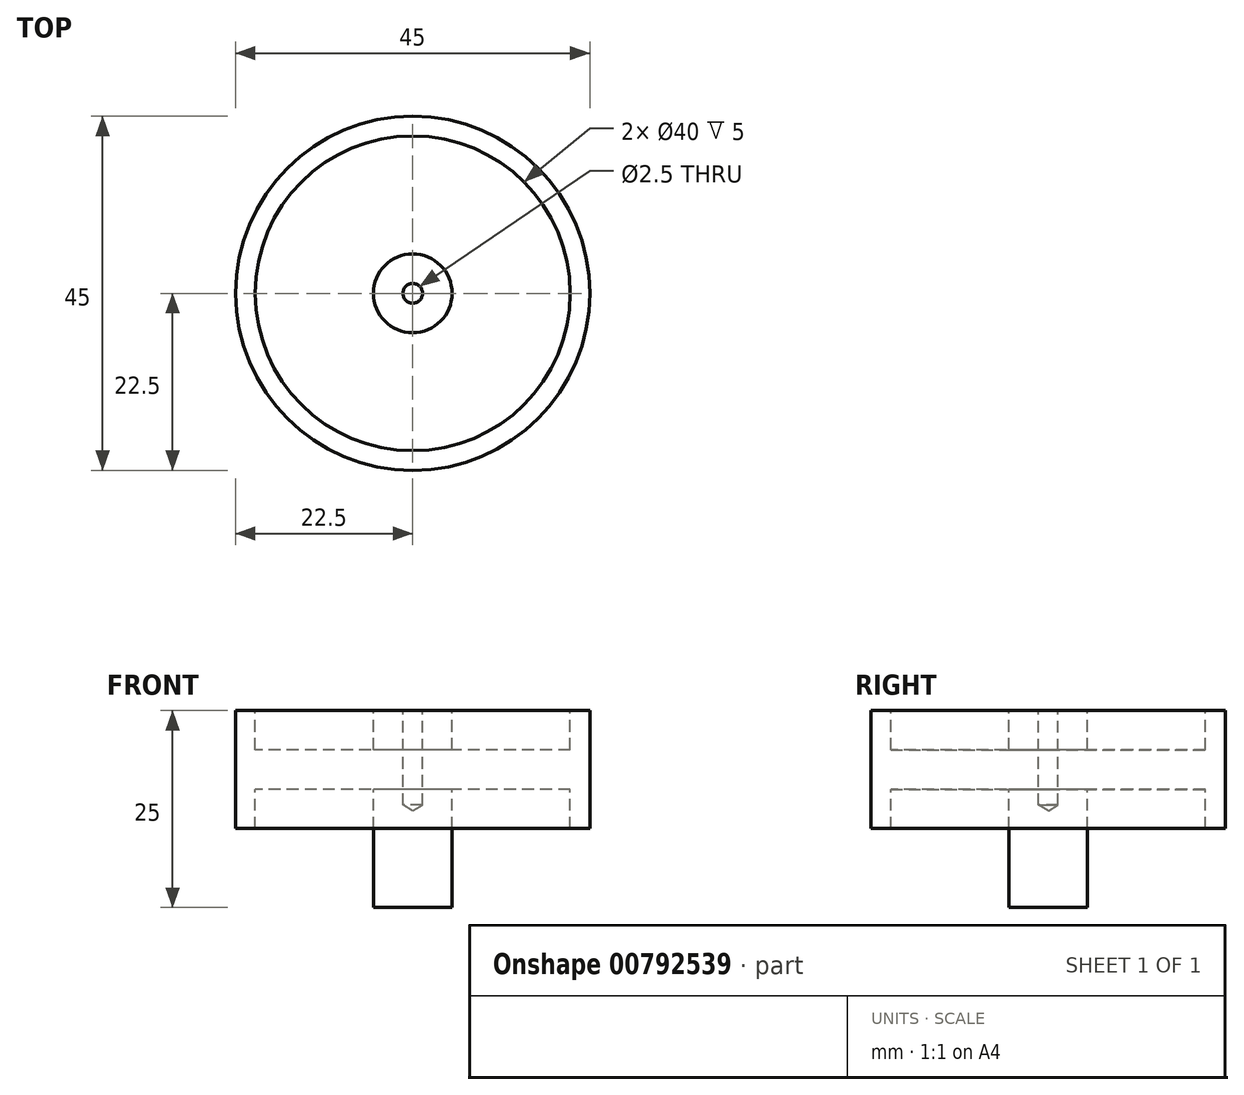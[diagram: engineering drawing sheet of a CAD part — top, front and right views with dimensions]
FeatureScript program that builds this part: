
annotation { "Feature Type Name" : "Feature", "Feature Type Description" : "" }
export const myFeature = defineFeature(function(context is Context, id is Id, definition is map)
    precondition{}
    {
        {
            var Q0;
            Q0=qCreatedBy(makeId("Top.planeOp"),FACE);
            var sketch = newSketch(context, id + "F0", { "sketchPlane" : qUnion([Q0])});
            skCircle(sketch, "E0", {"center": v(0, 0) * mm, "radius": 22.5 * mm});
            skCircle(sketch, "E1", {"center": v(0, 0) * mm, "radius": 20 * mm});
            skCircle(sketch, "E2", {"center": v(0, 0) * mm, "radius": 5 * mm});
            skCircle(sketch, "E3", {"center": v(0, 0) * mm, "radius": 1.25 * mm});
            skSolve(sketch);
        }
        {
            var Q0;
            Q0=makeQuery(id+"F0.imprint","IMPRINT",FACE,{"disambiguationData":[TD([[makeQuery(id+"F0.imprint","IMPRINT",EDGE,{"derivedFrom":sQuery(id+"F0.wireOp",EDGE,"E0")}),1.0]])]});
            extrude(context, id + "F1", {"entities" : qUnion([Q0]), "oppositeDirection" : true, "depth" : 15 * mm, "offsetDistance" : 25 * mm});
        }
        {
            var Q0;
            Q0=makeQuery(id+"F0.imprint","IMPRINT",FACE,{"disambiguationData":[TD([[makeQuery(id+"F0.imprint","IMPRINT",EDGE,{"derivedFrom":sQuery(id+"F0.wireOp",EDGE,"E1")}),1.0]])]});
            extrude(context, id + "F2", {"entities" : qUnion([Q0]), "operationType" : NewBodyOperationType.ADD, "oppositeDirection" : true, "depth" : 10 * mm, "offsetDistance" : 25 * mm});
        }
        {
            var Q0;
            Q0=makeQuery(id+"F0.imprint","IMPRINT",FACE,{"disambiguationData":[TD([[makeQuery(id+"F0.imprint","IMPRINT",EDGE,{"derivedFrom":sQuery(id+"F0.wireOp",EDGE,"E1")}),1.0]])]});
            extrude(context, id + "F3", {"entities" : qUnion([Q0]), "operationType" : NewBodyOperationType.REMOVE, "oppositeDirection" : true, "depth" : 5 * mm, "offsetDistance" : 25 * mm});
        }
        {
            var Q0;
            Q0=makeQuery(id+"F0.imprint","IMPRINT",FACE,{"disambiguationData":[TD([[makeQuery(id+"F0.imprint","IMPRINT",EDGE,{"derivedFrom":sQuery(id+"F0.wireOp",EDGE,"E2")}),1.0]])]});
            var Q1;
            Q1=makeQuery(id+"F0.imprint","IMPRINT",FACE,{"disambiguationData":[TD([[makeQuery(id+"F0.imprint","IMPRINT",EDGE,{"derivedFrom":sQuery(id+"F0.wireOp",EDGE,"E3")}),1.0]])]});
            extrude(context, id + "F4", {"entities" : qUnion([Q0, Q1]), "operationType" : NewBodyOperationType.ADD, "oppositeDirection" : true, "depth" : 25 * mm, "offsetDistance" : 25 * mm});
        }
        {
            var Q0;
            Q0=sQuery(id+"F0.wireOp",VERTEX,"E0.center");
            var Q1;
            Q1=makeQuery(id+"F1.opExtrude","SWEPT_BODY",BODY,{"disambiguationData":[OSD([sQuery(id+"F0.wireOp",EDGE,"E0"),sQuery(id+"F0.wireOp",EDGE,"E1")])]});
            hole(context, id + "F5", {"style" : HoleStyle.SIMPLE, "endStyle" : HoleEndStyle.BLIND, "holeDiameter" : 2.5 * mm, "majorDiameter" : 5 * mm, "holeDepth" : 12 * mm, "isTappedThrough" : true, "tappedDepth" : 12 * mm, "tapClearance" : 3, "locations" : qUnion([Q0]), "scope" : qUnion([Q1])});
        }
    });
